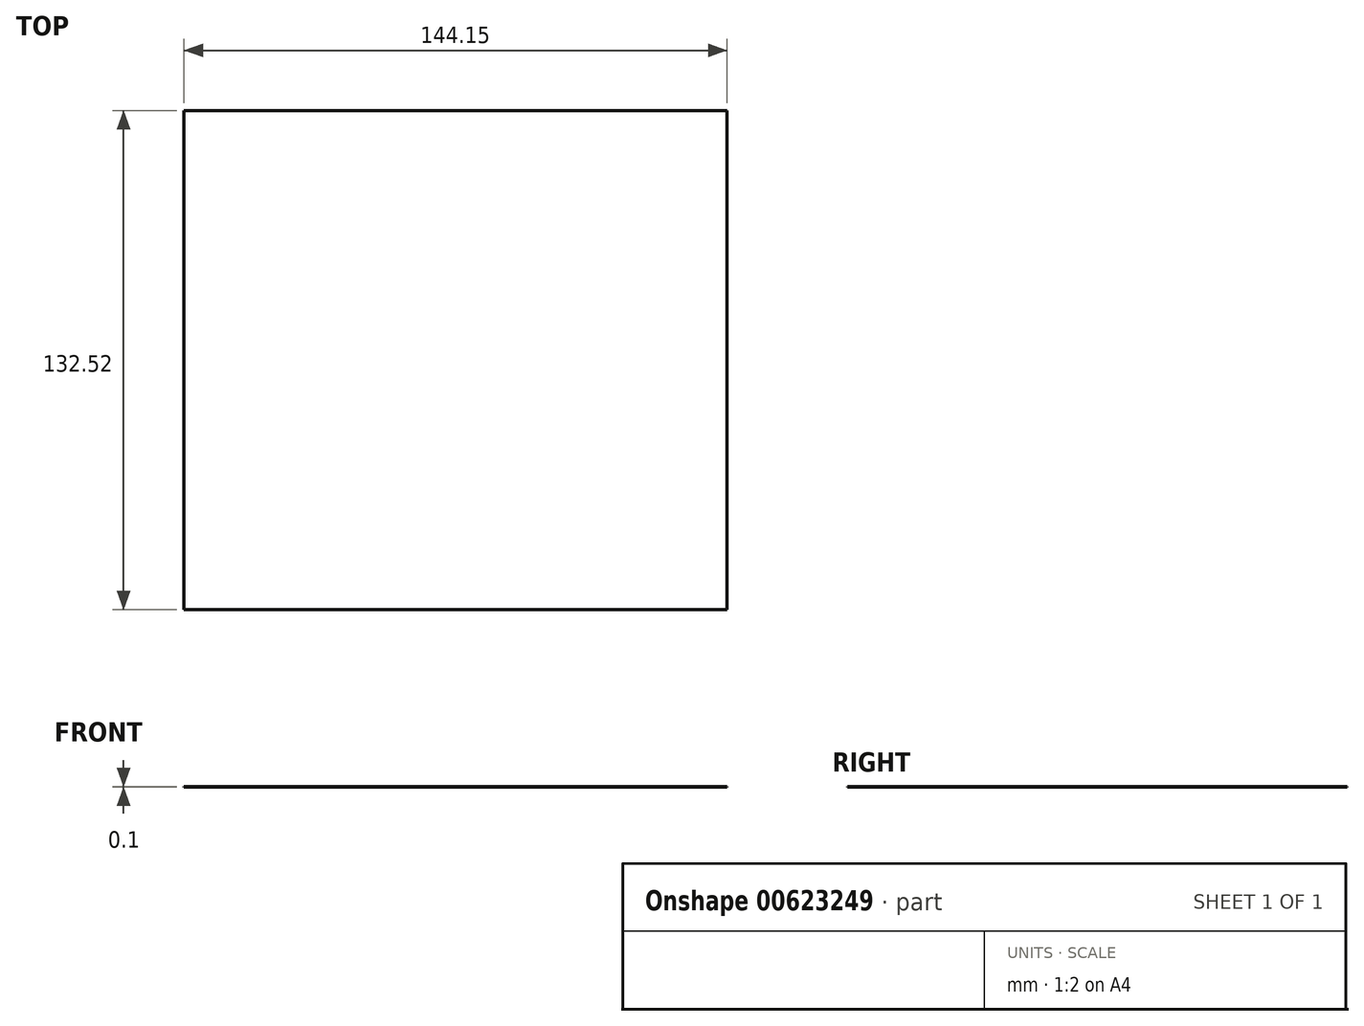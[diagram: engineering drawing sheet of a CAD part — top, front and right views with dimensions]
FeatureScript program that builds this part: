
annotation { "Feature Type Name" : "Feature", "Feature Type Description" : "" }
export const myFeature = defineFeature(function(context is Context, id is Id, definition is map)
    precondition{}
    {
        {
            var Q0;
            Q0=qCreatedBy(makeId("Top.planeOp"),FACE);
            var sketch = newSketch(context, id + "F0", { "sketchPlane" : qUnion([Q0])});
            skLineSegment(sketch, "E0.bottom", {"start": v(-68.84, 63.9) * mm, "end": v(75.3, 63.9) * mm});
            skLineSegment(sketch, "E0.top", {"start": v(-68.84, -68.62) * mm, "end": v(75.3, -68.62) * mm});
            skLineSegment(sketch, "E0.left", {"start": v(-68.84, 63.9) * mm, "end": v(-68.84, -68.62) * mm});
            skLineSegment(sketch, "E0.right", {"start": v(75.3, 63.9) * mm, "end": v(75.3, -68.62) * mm});
            skSolve(sketch);
        }
        {
            var Q0;
            Q0=makeQuery(id+"F0.imprint","IMPRINT",FACE,{"disambiguationData":[TD([[makeQuery(id+"F0.imprint","IMPRINT",EDGE,{"derivedFrom":sQuery(id+"F0.wireOp",EDGE,"E0.bottom")}),-1.0]])]});
            extrude(context, id + "F1", {"entities" : qUnion([Q0]), "depth" : 0.1 * mm, "offsetDistance" : 25 * mm});
        }
    });
